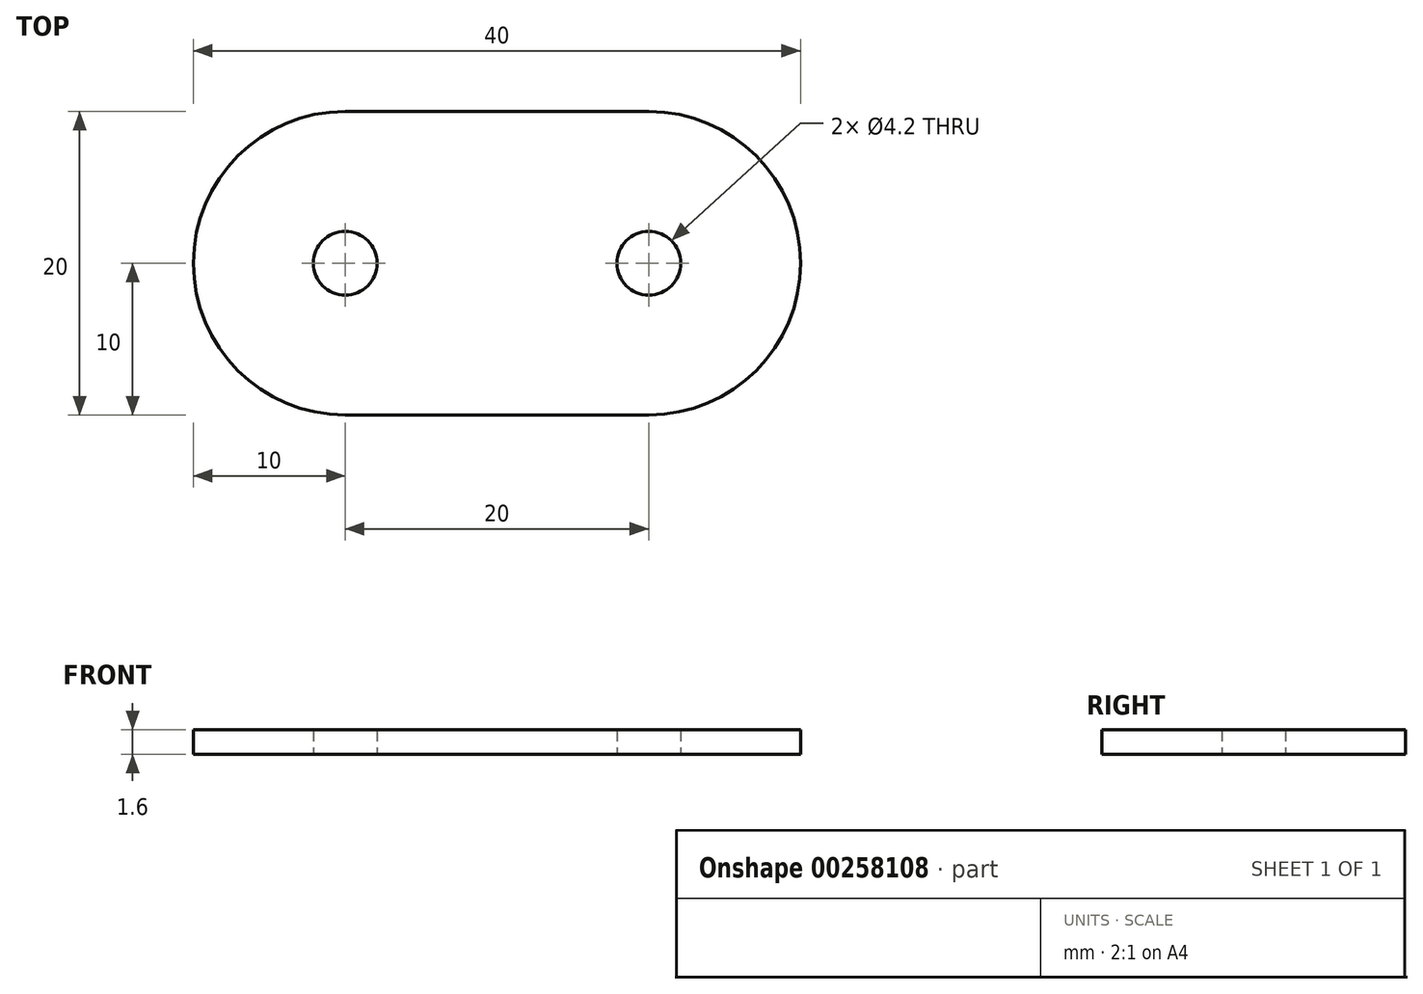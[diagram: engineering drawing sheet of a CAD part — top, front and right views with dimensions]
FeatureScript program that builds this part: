
annotation { "Feature Type Name" : "Feature", "Feature Type Description" : "" }
export const myFeature = defineFeature(function(context is Context, id is Id, definition is map)
    precondition{}
    {
        {
            var Q0;
            Q0=qCreatedBy(makeId("Top.planeOp"),FACE);
            var sketch = newSketch(context, id + "F0", { "sketchPlane" : qUnion([Q0])});
            skPoint(sketch, "E0.middle", {"position": v(0, 0) * mm});
            skCircle(sketch, "E1", {"center": v(-10, 0) * mm, "radius": 2.1 * mm});
            skCircle(sketch, "E2", {"center": v(10, 0) * mm, "radius": 2.1 * mm});
            skCircle(sketch, "E3", {"center": v(-10, 0) * mm, "radius": 10 * mm});
            skCircle(sketch, "E4", {"center": v(10, 0) * mm, "radius": 10 * mm});
            skLineSegment(sketch, "E5", {"start": v(-10, 10) * mm, "end": v(10, 10) * mm});
            skLineSegment(sketch, "E6", {"start": v(-10, -10) * mm, "end": v(10, -10) * mm});
            skSolve(sketch);
        }
        {
            var Q0;
            Q0=makeQuery(id+"F0.imprint","IMPRINT",FACE,{"disambiguationData":[TD([[makeQuery(id+"F0.imprint","IMPRINT",EDGE,{"derivedFrom":sQuery(id+"F0.wireOp",EDGE,"E0.bottom")}),1.0]])]});
            var Q1;
            Q1=makeQuery(id+"F0.imprint","IMPRINT",FACE,{"disambiguationData":[TD([[makeQuery(id+"F0.imprint","IMPRINT",EDGE,{"derivedFrom":sQuery(id+"F0.wireOp",EDGE,"E1")}),-1.0]])]});
            var Q2;
            Q2=makeQuery(id+"F0.imprint","IMPRINT",FACE,{"disambiguationData":[TD([[makeQuery(id+"F0.imprint","IMPRINT",EDGE,{"derivedFrom":sQuery(id+"F0.wireOp",EDGE,"E2")}),-1.0]])]});
            var Q3;
            {var subQ0=sQuery(id+"F0.wireOp",EDGE,"E5");Q3=makeQuery(id+"F0.imprint","IMPRINT",FACE,{"disambiguationData":[TD([[makeQuery(id+"F0.imprint","IMPRINT",EDGE,{"derivedFrom":subQ0}),-1.0]])]});}
            var Q4;
            {var subQ0=sQuery(id+"F0.wireOp",EDGE,"E6");Q4=makeQuery(id+"F0.imprint","IMPRINT",FACE,{"disambiguationData":[TD([[makeQuery(id+"F0.imprint","IMPRINT",EDGE,{"derivedFrom":subQ0}),1.0]])]});}
            extrude(context, id + "F1", {"entities" : qUnion([Q0, Q1, Q2, Q3, Q4]), "depth" : 1.6 * mm, "offsetDistance" : 25 * mm});
        }
    });
